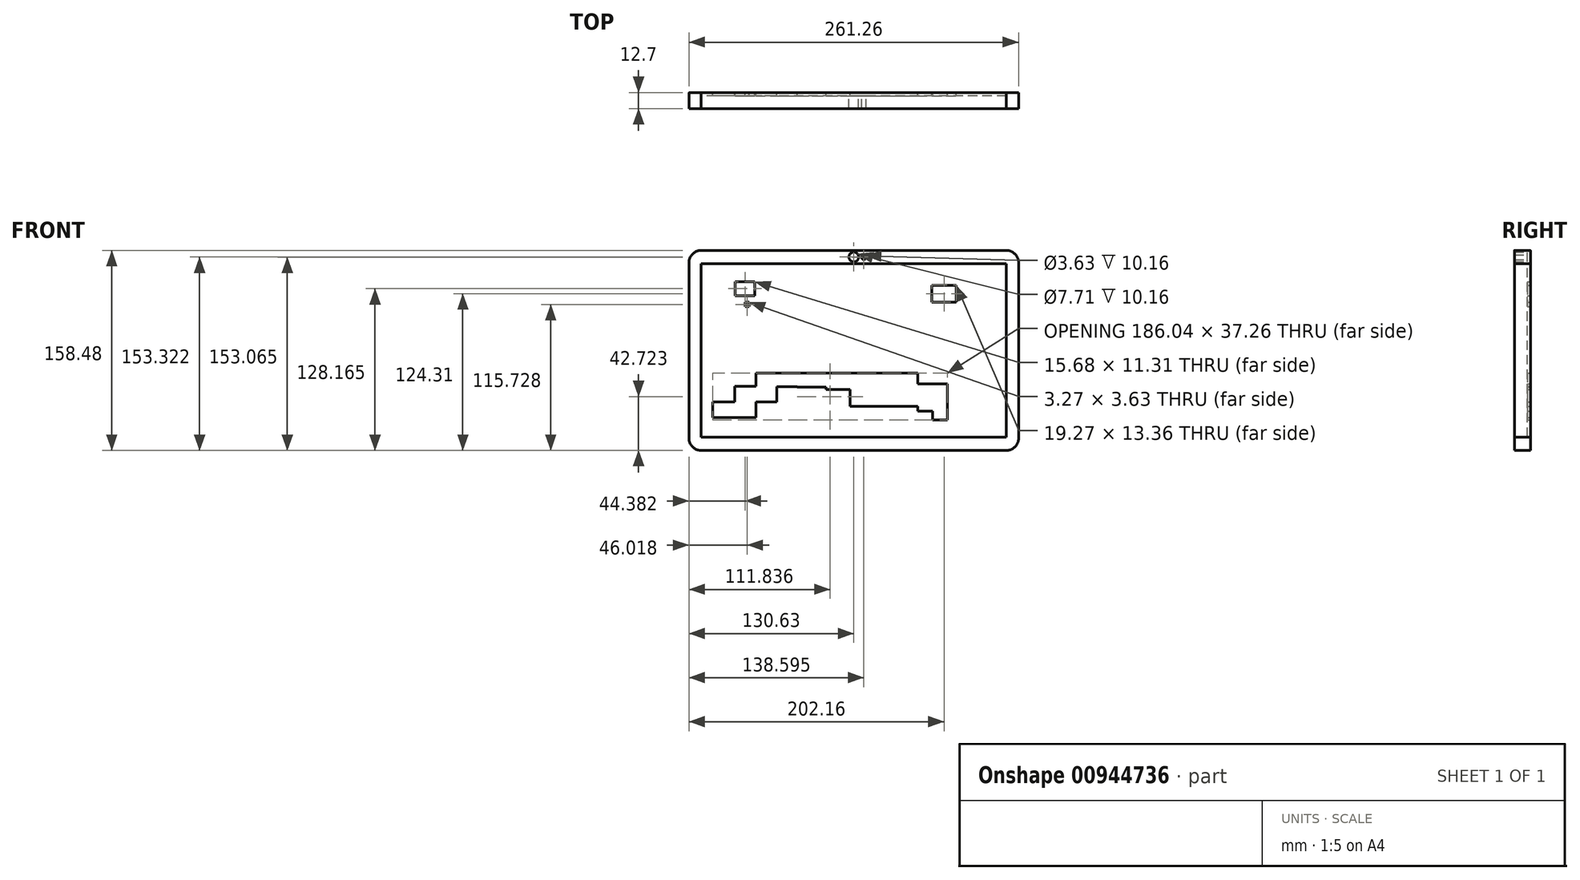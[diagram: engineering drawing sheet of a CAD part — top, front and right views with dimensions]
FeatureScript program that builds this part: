
annotation { "Feature Type Name" : "Feature", "Feature Type Description" : "" }
export const myFeature = defineFeature(function(context is Context, id is Id, definition is map)
    precondition{}
    {
        {
            var Q0;
            Q0=qCreatedBy(makeId("Front.planeOp"),FACE);
            var sketch = newSketch(context, id + "F0", { "sketchPlane" : qUnion([Q0])});
            skLineSegment(sketch, "E0.bottom", {"start": v(0, 0) * mm, "end": v(-120.96, 0) * mm});
            skLineSegment(sketch, "E0.top", {"start": v(0, 68.6) * mm, "end": v(-120.96, 68.6) * mm});
            skLineSegment(sketch, "E0.left", {"start": v(0, 0) * mm, "end": v(0, 68.6) * mm});
            skLineSegment(sketch, "E0.right", {"start": v(-120.96, 0) * mm, "end": v(-120.96, 68.6) * mm});
            skLineSegment(sketch, "E1.MirrorCS", {"start": v(0, 0) * mm, "end": v(120.96, 0) * mm});
            skLineSegment(sketch, "E2.MirrorCS", {"start": v(120.96, 0) * mm, "end": v(120.96, 68.6) * mm});
            skLineSegment(sketch, "E3.MirrorCS", {"start": v(0, 68.6) * mm, "end": v(120.96, 68.6) * mm});
            skLineSegment(sketch, "E4.MirrorCS", {"start": v(-120.96, 0) * mm, "end": v(-120.96, -68.6) * mm});
            skLineSegment(sketch, "E5.MirrorCS", {"start": v(0, -68.6) * mm, "end": v(-120.96, -68.6) * mm});
            skLineSegment(sketch, "E6.MirrorCS", {"start": v(0, 0) * mm, "end": v(0, -68.6) * mm});
            skLineSegment(sketch, "E7.MirrorCS", {"start": v(0, -68.6) * mm, "end": v(120.96, -68.6) * mm});
            skLineSegment(sketch, "E8.MirrorCS", {"start": v(120.96, 0) * mm, "end": v(120.96, -68.6) * mm});
            skLineSegment(sketch, "E9", {"start": v(-120.96, 68.6) * mm, "end": v(-120.96, 79.23) * mm});
            skLineSegment(sketch, "E10", {"start": v(-120.96, 68.6) * mm, "end": v(-130.56, 68.6) * mm});
            skArc(sketch, "E11", {"start": v(-120.96, 79.23) * mm, "mid": v(-128.16, 76.1) * mm, "end": v(-130.56, 68.6) * mm});
            skLineSegment(sketch, "E12.MirrorCS", {"start": v(120.96, 68.6) * mm, "end": v(120.96, 79.23) * mm});
            skArc(sketch, "E13.MirrorCS", {"start": v(120.96, 79.23) * mm, "mid": v(128.16, 76.1) * mm, "end": v(130.56, 68.6) * mm});
            skLineSegment(sketch, "E14.MirrorCS", {"start": v(120.96, 68.6) * mm, "end": v(130.56, 68.6) * mm});
            skLineSegment(sketch, "E15.MirrorCS", {"start": v(-120.96, -68.6) * mm, "end": v(-120.96, -79.23) * mm});
            skArc(sketch, "E16.MirrorCS", {"start": v(-120.96, -79.23) * mm, "mid": v(-128.16, -76.1) * mm, "end": v(-130.56, -68.6) * mm});
            skLineSegment(sketch, "E17.MirrorCS", {"start": v(-120.96, -68.6) * mm, "end": v(-130.56, -68.6) * mm});
            skLineSegment(sketch, "E18.MirrorCS", {"start": v(120.96, -68.6) * mm, "end": v(130.56, -68.6) * mm});
            skArc(sketch, "E19.MirrorCS", {"start": v(120.96, -79.23) * mm, "mid": v(128.16, -76.1) * mm, "end": v(130.56, -68.6) * mm});
            skLineSegment(sketch, "E20.MirrorCS", {"start": v(120.96, -68.6) * mm, "end": v(120.96, -79.23) * mm});
            skLineSegment(sketch, "E21", {"start": v(-120.96, 79.23) * mm, "end": v(120.96, 79.23) * mm});
            skLineSegment(sketch, "E22", {"start": v(-130.56, 68.6) * mm, "end": v(-130.56, -68.6) * mm});
            skLineSegment(sketch, "E23", {"start": v(-120.96, -79.23) * mm, "end": v(120.96, -79.23) * mm});
            skLineSegment(sketch, "E24", {"start": v(130.56, -68.6) * mm, "end": v(130.56, 68.6) * mm});
            skCircle(sketch, "E25", {"center": v(0, 74.08) * mm, "radius": 3.86 * mm});
            skCircle(sketch, "E26", {"center": v(7.97, 73.82) * mm, "radius": 1.82 * mm});
            skLineSegment(sketch, "E27.bottom", {"start": v(-94.09, 54.58) * mm, "end": v(-78.41, 54.58) * mm});
            skLineSegment(sketch, "E27.top", {"start": v(-94.09, 43.27) * mm, "end": v(-78.41, 43.27) * mm});
            skLineSegment(sketch, "E27.left", {"start": v(-94.09, 54.58) * mm, "end": v(-94.09, 43.27) * mm});
            skLineSegment(sketch, "E27.right", {"start": v(-78.41, 54.58) * mm, "end": v(-78.41, 43.27) * mm});
            skLineSegment(sketch, "E28.bottom", {"start": v(61.9, 51.75) * mm, "end": v(81.17, 51.75) * mm});
            skLineSegment(sketch, "E28.top", {"start": v(61.9, 38.39) * mm, "end": v(81.17, 38.39) * mm});
            skLineSegment(sketch, "E28.left", {"start": v(61.9, 51.75) * mm, "end": v(61.9, 38.39) * mm});
            skLineSegment(sketch, "E28.right", {"start": v(81.17, 51.75) * mm, "end": v(81.17, 38.39) * mm});
            skLineSegment(sketch, "E29.bottom", {"start": v(-77.64, -17.89) * mm, "end": v(-61.2, -17.89) * mm});
            skLineSegment(sketch, "E29.top", {"start": v(-77.64, -28.42) * mm, "end": v(-61.2, -28.42) * mm});
            skLineSegment(sketch, "E29.left", {"start": v(-77.64, -17.89) * mm, "end": v(-77.64, -28.42) * mm});
            skLineSegment(sketch, "E29.right", {"start": v(-61.2, -17.89) * mm, "end": v(-61.2, -28.42) * mm});
            skLineSegment(sketch, "E30.bottom", {"start": v(-61.2, -17.89) * mm, "end": v(-44.75, -17.89) * mm});
            skLineSegment(sketch, "E30.top", {"start": v(-61.2, -28.68) * mm, "end": v(-44.75, -28.68) * mm});
            skLineSegment(sketch, "E30.left", {"start": v(-61.2, -17.89) * mm, "end": v(-61.2, -28.68) * mm});
            skLineSegment(sketch, "E30.right", {"start": v(-44.75, -17.89) * mm, "end": v(-44.75, -28.68) * mm});
            skLineSegment(sketch, "E31.bottom", {"start": v(-77.64, -28.42) * mm, "end": v(-94.34, -28.42) * mm});
            skLineSegment(sketch, "E31.top", {"start": v(-77.64, -40.76) * mm, "end": v(-94.34, -40.76) * mm});
            skLineSegment(sketch, "E31.left", {"start": v(-77.64, -28.42) * mm, "end": v(-77.64, -40.76) * mm});
            skLineSegment(sketch, "E31.right", {"start": v(-94.34, -28.42) * mm, "end": v(-94.34, -40.76) * mm});
            skLineSegment(sketch, "E32.bottom", {"start": v(-94.34, -40.76) * mm, "end": v(-111.82, -40.76) * mm});
            skLineSegment(sketch, "E32.top", {"start": v(-94.34, -53.1) * mm, "end": v(-111.82, -53.1) * mm});
            skLineSegment(sketch, "E32.left", {"start": v(-94.34, -40.76) * mm, "end": v(-94.34, -53.1) * mm});
            skLineSegment(sketch, "E32.right", {"start": v(-111.82, -40.76) * mm, "end": v(-111.82, -53.1) * mm});
            skLineSegment(sketch, "E33.top", {"start": v(-77.64, -53.1) * mm, "end": v(-94.34, -53.1) * mm});
            skLineSegment(sketch, "E33.left", {"start": v(-77.64, -40.76) * mm, "end": v(-77.64, -53.1) * mm});
            skLineSegment(sketch, "E34.bottom", {"start": v(-61.2, -28.42) * mm, "end": v(-77.64, -28.42) * mm});
            skLineSegment(sketch, "E34.top", {"start": v(-61.2, -40.76) * mm, "end": v(-77.64, -40.76) * mm});
            skLineSegment(sketch, "E34.left", {"start": v(-61.2, -28.42) * mm, "end": v(-61.2, -40.76) * mm});
            skLineSegment(sketch, "E35.left", {"start": v(-44.75, -17.89) * mm, "end": v(-44.75, -17.89) * mm});
            skLineSegment(sketch, "E36.bottom", {"start": v(-44.75, -17.89) * mm, "end": v(-22.13, -17.89) * mm});
            skLineSegment(sketch, "E36.top", {"start": v(-44.75, -28.94) * mm, "end": v(-22.13, -28.94) * mm});
            skLineSegment(sketch, "E36.left", {"start": v(-44.75, -17.89) * mm, "end": v(-44.75, -28.94) * mm});
            skLineSegment(sketch, "E36.right", {"start": v(-22.13, -17.89) * mm, "end": v(-22.13, -28.94) * mm});
            skLineSegment(sketch, "E37.bottom", {"start": v(-22.13, -17.89) * mm, "end": v(-2.86, -17.89) * mm});
            skLineSegment(sketch, "E37.top", {"start": v(-22.13, -31) * mm, "end": v(-2.86, -31) * mm});
            skLineSegment(sketch, "E37.left", {"start": v(-22.13, -17.89) * mm, "end": v(-22.13, -31) * mm});
            skLineSegment(sketch, "E37.right", {"start": v(-2.86, -17.89) * mm, "end": v(-2.86, -31) * mm});
            skLineSegment(sketch, "E38.bottom", {"start": v(-2.86, -31) * mm, "end": v(20.52, -31) * mm});
            skLineSegment(sketch, "E38.top", {"start": v(-2.86, -44.35) * mm, "end": v(20.52, -44.35) * mm});
            skLineSegment(sketch, "E38.left", {"start": v(-2.86, -31) * mm, "end": v(-2.86, -44.35) * mm});
            skLineSegment(sketch, "E38.right", {"start": v(20.52, -31) * mm, "end": v(20.52, -44.35) * mm});
            skLineSegment(sketch, "E39.bottom", {"start": v(-2.86, -17.89) * mm, "end": v(23.6, -17.89) * mm});
            skLineSegment(sketch, "E39.top", {"start": v(-2.86, -31) * mm, "end": v(23.6, -31) * mm});
            skLineSegment(sketch, "E39.right", {"start": v(23.6, -17.89) * mm, "end": v(23.6, -31) * mm});
            skLineSegment(sketch, "E40.bottom", {"start": v(23.6, -31) * mm, "end": v(27.97, -31) * mm});
            skLineSegment(sketch, "E40.top", {"start": v(23.6, -34.33) * mm, "end": v(27.97, -34.33) * mm});
            skLineSegment(sketch, "E40.left", {"start": v(23.6, -31) * mm, "end": v(23.6, -34.33) * mm});
            skLineSegment(sketch, "E40.right", {"start": v(27.97, -31) * mm, "end": v(27.97, -34.33) * mm});
            skLineSegment(sketch, "E41.bottom", {"start": v(23.6, -17.89) * mm, "end": v(50.59, -17.89) * mm});
            skLineSegment(sketch, "E41.top", {"start": v(23.6, -31) * mm, "end": v(50.59, -31) * mm});
            skLineSegment(sketch, "E41.right", {"start": v(50.59, -17.89) * mm, "end": v(50.59, -31) * mm});
            skLineSegment(sketch, "E42.bottom", {"start": v(20.52, -44.35) * mm, "end": v(51.1, -44.35) * mm});
            skLineSegment(sketch, "E42.top", {"start": v(20.52, -36.39) * mm, "end": v(51.1, -36.39) * mm});
            skLineSegment(sketch, "E42.left", {"start": v(20.52, -44.35) * mm, "end": v(20.52, -36.39) * mm});
            skLineSegment(sketch, "E42.right", {"start": v(51.1, -44.35) * mm, "end": v(51.1, -36.39) * mm});
            skLineSegment(sketch, "E43.bottom", {"start": v(50.59, -26.62) * mm, "end": v(74.23, -26.62) * mm});
            skLineSegment(sketch, "E43.top", {"start": v(50.59, -47.95) * mm, "end": v(74.23, -47.95) * mm});
            skLineSegment(sketch, "E43.left", {"start": v(50.59, -26.62) * mm, "end": v(50.59, -47.95) * mm});
            skLineSegment(sketch, "E43.right", {"start": v(74.23, -26.62) * mm, "end": v(74.23, -47.95) * mm});
            skLineSegment(sketch, "E44.bottom", {"start": v(62.4, -47.95) * mm, "end": v(74.23, -47.95) * mm});
            skLineSegment(sketch, "E44.top", {"start": v(62.4, -55.15) * mm, "end": v(74.23, -55.15) * mm});
            skLineSegment(sketch, "E44.left", {"start": v(62.4, -47.95) * mm, "end": v(62.4, -55.15) * mm});
            skLineSegment(sketch, "E44.right", {"start": v(74.23, -47.95) * mm, "end": v(74.23, -55.15) * mm});
            skPoint(sketch, "E45.firstSnap0", {"position": v(-86.25, 43.27) * mm});
            skLineSegment(sketch, "E45.bottom", {"start": v(-86.25, 38.3) * mm, "end": v(-82.98, 38.3) * mm});
            skLineSegment(sketch, "E45.top", {"start": v(-86.25, 34.67) * mm, "end": v(-82.98, 34.67) * mm});
            skLineSegment(sketch, "E45.left", {"start": v(-86.25, 38.3) * mm, "end": v(-86.25, 34.67) * mm});
            skLineSegment(sketch, "E45.right", {"start": v(-82.98, 38.3) * mm, "end": v(-82.98, 34.67) * mm});
            skSolve(sketch);
        }
        {
            var Q0;
            {var subQ0=makeQuery(id+"F0.imprint","IMPRINT",EDGE,{"derivedFrom":sQuery(id+"F0.wireOp",EDGE,"E12.MirrorCS")});var subQ1=makeQuery(id+"F0.imprint","IMPRINT",EDGE,{"derivedFrom":sQuery(id+"F0.wireOp",EDGE,"E9")});var subQ3=makeQuery(id+"F0.imprint","IMPRINT",EDGE,{"derivedFrom":sQuery(id+"F0.wireOp",EDGE,"E15.MirrorCS")});var subQ4=makeQuery(id+"F0.imprint","IMPRINT",EDGE,{"derivedFrom":sQuery(id+"F0.wireOp",EDGE,"E18.MirrorCS")});Q0=qUnion([makeQuery(id+"F0.imprint","IMPRINT",FACE,{"disambiguationData":[TD([[subQ1,1.0]])]}),makeQuery(id+"F0.imprint","IMPRINT",FACE,{"disambiguationData":[TD([[subQ0,-1.0]])]}),makeQuery(id+"F0.imprint","IMPRINT",FACE,{"disambiguationData":[TD([[subQ3,-1.0]])]}),makeQuery(id+"F0.imprint","IMPRINT",FACE,{"disambiguationData":[TD([[subQ4,-1.0]])]}),makeQuery(id+"F0.imprint","IMPRINT",FACE,{"disambiguationData":[TD([[makeQuery(id+"F0.imprint","IMPRINT",EDGE,{"derivedFrom":sQuery(id+"F0.wireOp",EDGE,"E0.right")}),1.0]])]}),makeQuery(id+"F0.imprint","IMPRINT",FACE,{"disambiguationData":[TD([[makeQuery(id+"F0.imprint","IMPRINT",EDGE,{"derivedFrom":sQuery(id+"F0.wireOp",EDGE,"E2.MirrorCS")}),-1.0]])]}),makeQuery(id+"F0.imprint","IMPRINT",FACE,{"disambiguationData":[TD([[makeQuery(id+"F0.imprint","IMPRINT",EDGE,{"derivedFrom":sQuery(id+"F0.wireOp",EDGE,"E5.MirrorCS")}),1.0]])]}),makeQuery(id+"F0.imprint","IMPRINT",FACE,{"disambiguationData":[TD([[makeQuery(id+"F0.imprint","IMPRINT",EDGE,{"derivedFrom":sQuery(id+"F0.wireOp",EDGE,"E0.top")}),-1.0]])]})]);}
            extrude(context, id + "F1", {"entities" : qUnion([Q0]), "depth" : 12.7 * mm, "offsetDistance" : 25.4 * mm});
        }
        {
            var Q0;
            Q0=makeQuery(id+"F0.imprint","IMPRINT",FACE,{"disambiguationData":[TD([[makeQuery(id+"F0.imprint","IMPRINT",EDGE,{"derivedFrom":sQuery(id+"F0.wireOp",EDGE,"E0.bottom")}),-1.0]])]});
            var Q1;
            Q1=makeQuery(id+"F0.imprint","IMPRINT",FACE,{"disambiguationData":[TD([[makeQuery(id+"F0.imprint","IMPRINT",EDGE,{"derivedFrom":sQuery(id+"F0.wireOp",EDGE,"E0.left")}),-1.0]])]});
            var Q2;
            {var subQ11=sQuery(id+"F0.wireOp",EDGE,"E1.MirrorCS");Q2=makeQuery(id+"F0.imprint","IMPRINT",FACE,{"disambiguationData":[TD([[makeQuery(id+"F0.imprint","IMPRINT",EDGE,{"derivedFrom":subQ11}),-1.0]])]});}
            var Q3;
            {var subQ2=sQuery(id+"F0.wireOp",EDGE,"E0.bottom");Q3=makeQuery(id+"F0.imprint","IMPRINT",FACE,{"disambiguationData":[TD([[makeQuery(id+"F0.imprint","IMPRINT",EDGE,{"derivedFrom":subQ2}),1.0]])]});}
            var Q4;
            Q4=makeQuery(id+"F0.imprint","IMPRINT",FACE,{"disambiguationData":[TD([[makeQuery(id+"F0.imprint","IMPRINT",EDGE,{"derivedFrom":sQuery(id+"F0.wireOp",EDGE,"E25")}),1.0]])]});
            var Q5;
            Q5=makeQuery(id+"F0.imprint","IMPRINT",FACE,{"disambiguationData":[TD([[makeQuery(id+"F0.imprint","IMPRINT",EDGE,{"derivedFrom":sQuery(id+"F0.wireOp",EDGE,"E26")}),1.0]])]});
            extrude(context, id + "F2", {"entities" : qUnion([Q0, Q1, Q2, Q3, Q4, Q5]), "operationType" : NewBodyOperationType.ADD, "depth" : 2.54 * mm, "offsetDistance" : 25.4 * mm});
        }
    });
